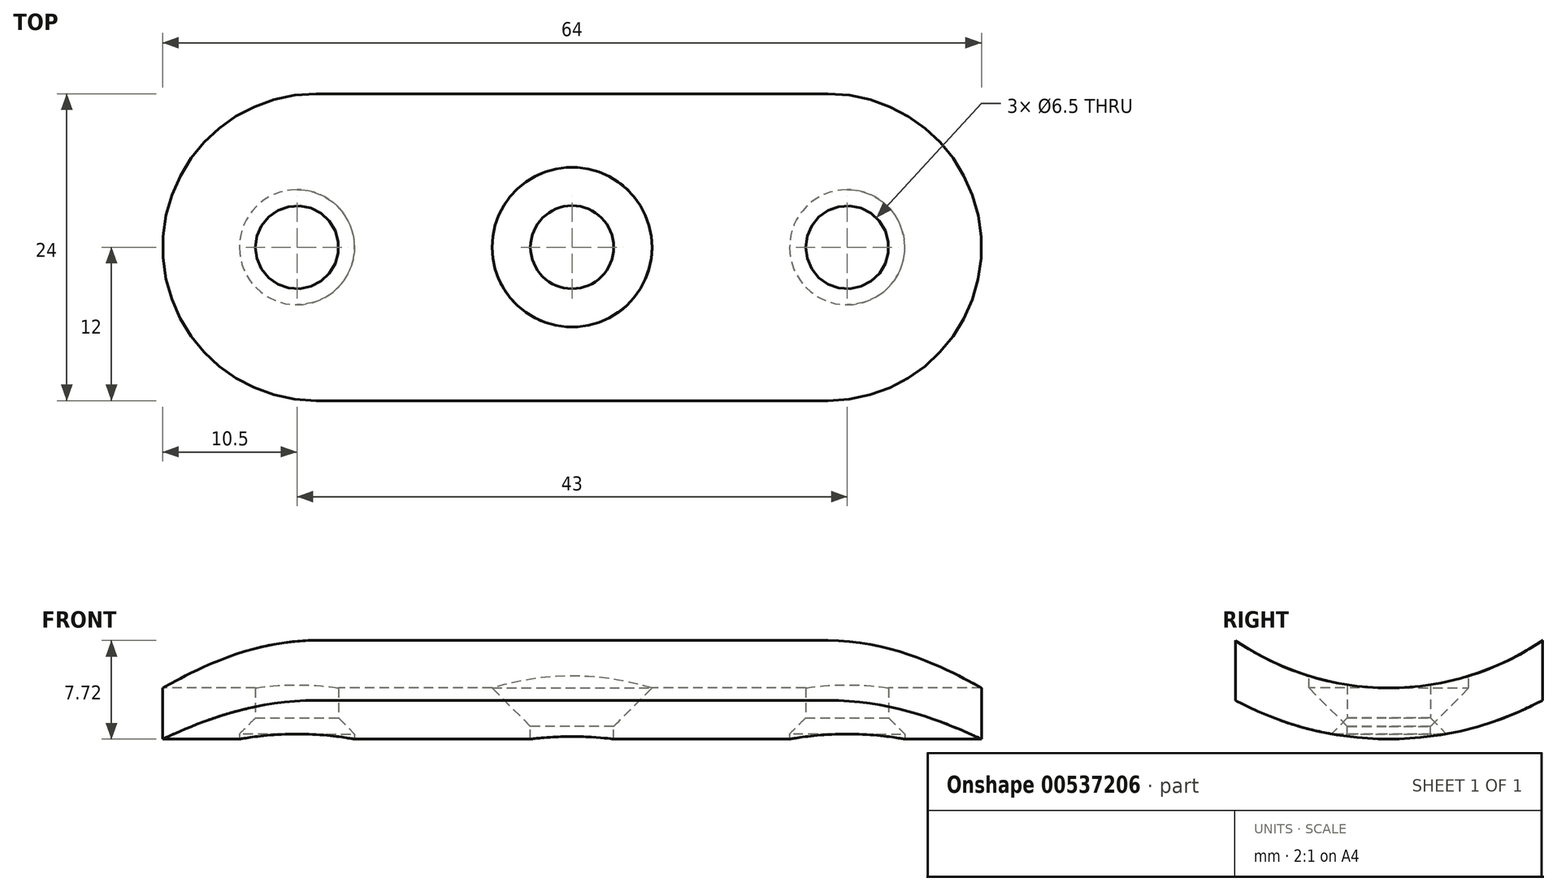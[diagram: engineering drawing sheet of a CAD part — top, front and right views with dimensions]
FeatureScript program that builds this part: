
annotation { "Feature Type Name" : "Feature", "Feature Type Description" : "" }
export const myFeature = defineFeature(function(context is Context, id is Id, definition is map)
    precondition{}
    {
        {
            var Q0;
            Q0=qCreatedBy(makeId("Top.planeOp"),FACE);
            var sketch = newSketch(context, id + "F0", { "sketchPlane" : qUnion([Q0])});
            skLineSegment(sketch, "E0", {"start": v(-20, -12) * mm, "end": v(20, -12) * mm});
            skArc(sketch, "E1", {"start": v(20, -12) * mm, "mid": v(32, 0) * mm, "end": v(20, 12) * mm});
            skLineSegment(sketch, "E2", {"start": v(20, 12) * mm, "end": v(-20, 12) * mm});
            skArc(sketch, "E3", {"start": v(-20, 12) * mm, "mid": v(-32, 0) * mm, "end": v(-20, -12) * mm});
            skSolve(sketch);
        }
        {
            var Q0;
            Q0=makeQuery(id+"F0.imprint","IMPRINT",FACE,{"disambiguationData":[TD([[makeQuery(id+"F0.imprint","IMPRINT",EDGE,{"derivedFrom":sQuery(id+"F0.wireOp",EDGE,"E0")}),1.0]])]});
            extrude(context, id + "F1", {"entities" : qUnion([Q0]), "depth" : 20 * mm, "offsetDistance" : 25 * mm});
        }
        {
            var Q0;
            Q0=qCreatedBy(makeId("Right.planeOp"),FACE);
            var sketch = newSketch(context, id + "F2", { "sketchPlane" : qUnion([Q0])});
            skArc(sketch, "E4", {"start": v(-15, 10.22) * mm, "mid": v(0, 4) * mm, "end": v(15, 10.22) * mm});
            skArc(sketch, "E5", {"start": v(-15, 4.95) * mm, "mid": v(0, 0) * mm, "end": v(15, 4.95) * mm});
            skLineSegment(sketch, "E6", {"start": v(-15, 10.22) * mm, "end": v(-15, 4.95) * mm});
            skLineSegment(sketch, "E7", {"start": v(15, 10.22) * mm, "end": v(15, 4.95) * mm});
            skSolve(sketch);
        }
        {
            var Q0;
            Q0=makeQuery(id+"F2.imprint","IMPRINT",FACE,{"disambiguationData":[TD([[makeQuery(id+"F2.imprint","IMPRINT",EDGE,{"derivedFrom":sQuery(id+"F2.wireOp",EDGE,"E4")}),-1.0]])]});
            extrude(context, id + "F3", {"entities" : qUnion([Q0]), "operationType" : NewBodyOperationType.INTERSECT, "endBound" : BoundingType.SYMMETRIC, "depth" : 80 * mm, "offsetDistance" : 25 * mm});
        }
        {
            var Q0;
            Q0=qCreatedBy(makeId("Top.planeOp"),FACE);
            var sketch = newSketch(context, id + "F4", { "sketchPlane" : qUnion([Q0])});
            skPoint(sketch, "E8", {"position": v(21.5, 0) * mm});
            skPoint(sketch, "E9", {"position": v(-21.5, 0) * mm});
            skSolve(sketch);
        }
        {
            var Q0;
            Q0=sQuery(id+"F4.wireOp",VERTEX,"E9");
            var Q1;
            Q1=sQuery(id+"F4.wireOp",VERTEX,"E8");
            var Q2;
            Q2=makeQuery(id+"F1.opExtrude","SWEPT_BODY",BODY,{"disambiguationData":[OSD([sQuery(id+"F0.wireOp",EDGE,"E0"),sQuery(id+"F0.wireOp",EDGE,"E1"),sQuery(id+"F0.wireOp",EDGE,"E2"),sQuery(id+"F0.wireOp",EDGE,"E3")])]});
            hole(context, id + "F5", {"style" : HoleStyle.C_SINK, "endStyle" : HoleEndStyle.THROUGH, "oppositeDirection" : true, "holeDiameter" : 6.5 * mm, "cSinkDiameter" : 9 * mm, "cSinkAngle" : 90 * degree, "isTappedThrough" : true, "tappedDepth" : 12 * mm, "tapClearance" : 3, "locations" : qUnion([Q0, Q1]), "scope" : qUnion([Q2])});
        }
        {
            var Q0;
            Q0=qCreatedBy(makeId("Top.planeOp"),FACE);
            cPlane(context, id + "F6", {"entities" : qUnion([Q0]), "cplaneType" : CPlaneType.OFFSET, "offset" : 5 * mm, "width" : 150 * mm, "height" : 150 * mm});
        }
        {
            var Q0;
            Q0=qCreatedBy(id+"F6.planeOp",FACE);
            var sketch = newSketch(context, id + "F7", { "sketchPlane" : qUnion([Q0])});
            skPoint(sketch, "E10", {"position": v(0, 0) * mm});
            skSolve(sketch);
        }
        {
            var Q0;
            Q0=sQuery(id+"F7.wireOp",VERTEX,"E10");
            var Q1;
            Q1=makeQuery(id+"F1.opExtrude","SWEPT_BODY",BODY,{"disambiguationData":[OSD([sQuery(id+"F0.wireOp",EDGE,"E0"),sQuery(id+"F0.wireOp",EDGE,"E1"),sQuery(id+"F0.wireOp",EDGE,"E2"),sQuery(id+"F0.wireOp",EDGE,"E3")])]});
            hole(context, id + "F8", {"style" : HoleStyle.C_SINK, "endStyle" : HoleEndStyle.THROUGH, "holeDiameter" : 6.5 * mm, "cSinkDiameter" : 12.5 * mm, "cSinkAngle" : 90 * degree, "isTappedThrough" : true, "tappedDepth" : 12 * mm, "tapClearance" : 3, "locations" : qUnion([Q0]), "scope" : qUnion([Q1])});
        }
    });
